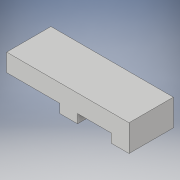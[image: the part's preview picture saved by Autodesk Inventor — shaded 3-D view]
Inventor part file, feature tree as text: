
AUTODESK INVENTOR PART (.ipt)
format: ipt  version: 2019 (Build 230136000, 136)  size: 102,912 bytes
history: native  units: mm
features: extrude x1, sketch x1
ambient origin geometry x8: Origin, YZ Plane, XZ Plane, XY Plane, X Axis, Y Axis, Z Axis, Center Point
bodies: Solid1 (feature_tree)
feature tree (2):
  extrude  "Extrusion1"  Depth=59.0mm
  sketch  "Sketch1"  dims[d0=19.0mm d1=10.0mm d2=10.0mm d3=30.0mm d4=10.0mm d5=5.0mm d6=59.0mm d7=10.0mm d8=10.0mm d9=59.0mm d10=25.0mm d11=0.0mm]
